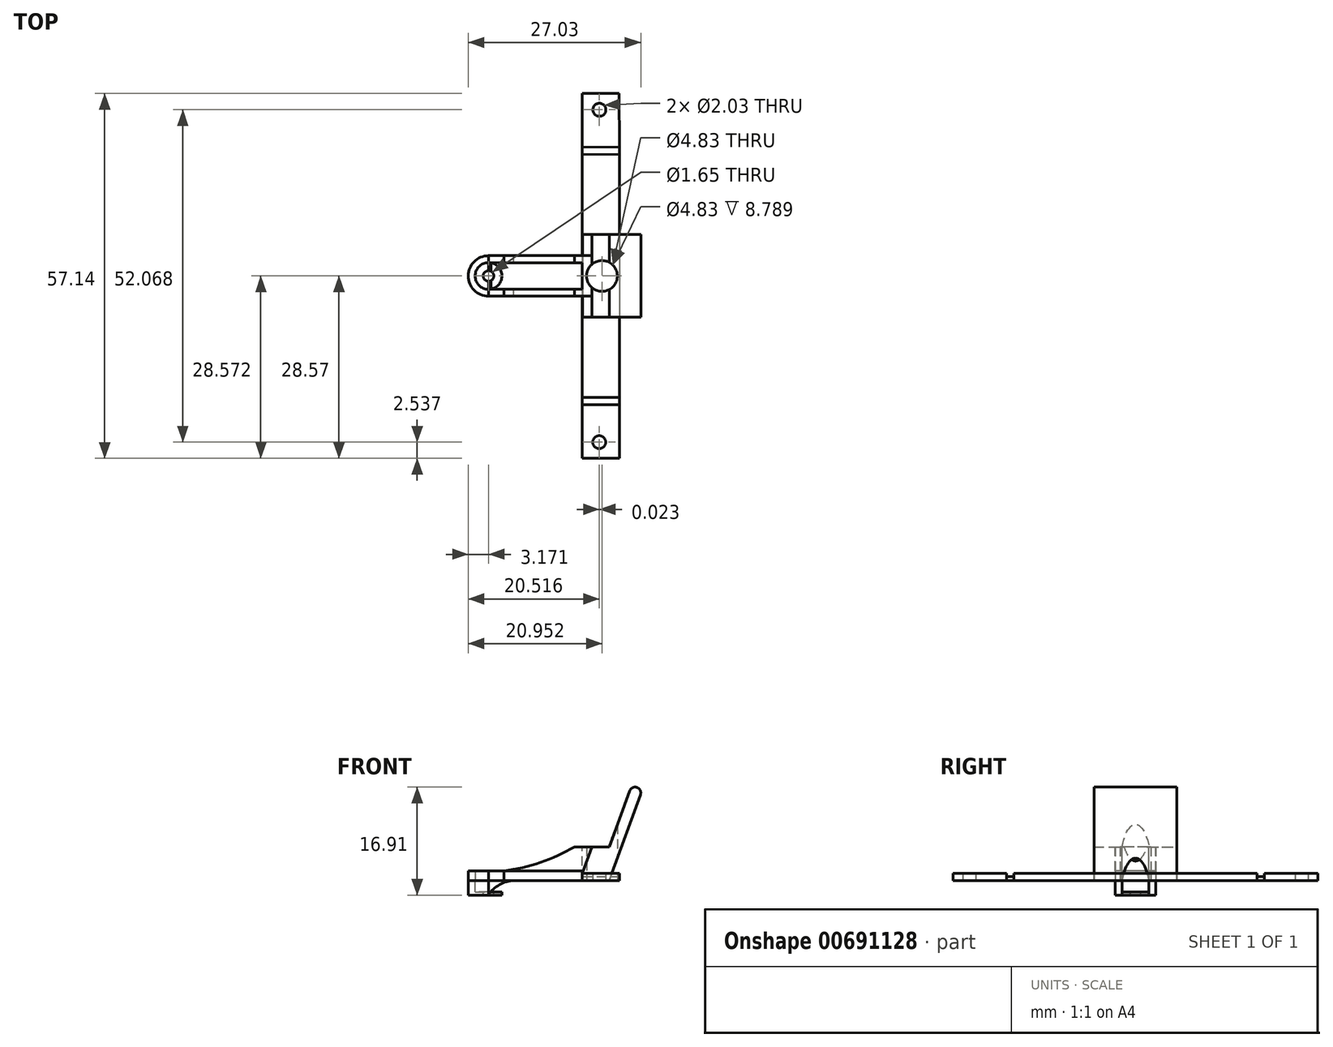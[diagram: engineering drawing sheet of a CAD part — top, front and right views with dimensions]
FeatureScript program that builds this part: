
annotation { "Feature Type Name" : "Feature", "Feature Type Description" : "" }
export const myFeature = defineFeature(function(context is Context, id is Id, definition is map)
    precondition{}
    {
        {
            var Q0;
            Q0=qCreatedBy(makeId("Top.planeOp"),FACE);
            var sketch = newSketch(context, id + "F0", { "sketchPlane" : qUnion([Q0])});
            skArc(sketch, "E0", {"start": v(-9.2, 3.18) * mm, "mid": v(-12.38, 0) * mm, "end": v(-9.2, -3.18) * mm});
            skCircle(sketch, "E1", {"center": v(-9.2, 0) * mm, "radius": 2.1 * mm});
            skLineSegment(sketch, "E2", {"start": v(11.34, 14.51) * mm, "end": v(11.34, -21.1) * mm});
            skLineSegment(sketch, "E3", {"start": v(5.47, 17.15) * mm, "end": v(5.47, -18.87) * mm});
            skCircle(sketch, "E4", {"center": v(-9.2, 0) * mm, "radius": 0.83 * mm});
            skLineSegment(sketch, "E5", {"start": v(-9.2, -3.17) * mm, "end": v(5.47, -3.17) * mm});
            skLineSegment(sketch, "E6", {"start": v(-9.2, 3.17) * mm, "end": v(5.47, 3.17) * mm});
            skLineSegment(sketch, "E7.trimOffspring", {"start": v(-6.81, -2.08) * mm, "end": v(5.47, -2.08) * mm});
            skLineSegment(sketch, "E8.trimOffspring", {"start": v(-6.81, 2.08) * mm, "end": v(5.47, 2.08) * mm});
            skPoint(sketch, "E9.start.orphan", {"position": v(-9.2, 2.1) * mm});
            skPoint(sketch, "E10.start.orphan", {"position": v(-9.2, -2.1) * mm});
            skCircle(sketch, "E11", {"center": v(8.57, 0) * mm, "radius": 2.41 * mm});
            skLineSegment(sketch, "E12", {"start": v(5.47, 17.15) * mm, "end": v(5.47, 28.57) * mm});
            skLineSegment(sketch, "E13", {"start": v(5.47, 28.57) * mm, "end": v(11.23, 28.57) * mm});
            skLineSegment(sketch, "E14", {"start": v(11.23, 28.57) * mm, "end": v(11.34, 14.51) * mm});
            skCircle(sketch, "E15", {"center": v(8.16, 26.03) * mm, "radius": 1.02 * mm});
            skLineSegment(sketch, "E16", {"start": v(5.47, -18.87) * mm, "end": v(5.47, -28.57) * mm});
            skLineSegment(sketch, "E17", {"start": v(5.47, -28.57) * mm, "end": v(11.34, -28.57) * mm});
            skLineSegment(sketch, "E18", {"start": v(11.34, -28.57) * mm, "end": v(11.34, -21.1) * mm});
            skCircle(sketch, "E19", {"center": v(8.14, -26.03) * mm, "radius": 1.02 * mm});
            skLineSegment(sketch, "E20", {"start": v(5.47, -19.05) * mm, "end": v(11.34, -19.05) * mm});
            skLineSegment(sketch, "E21", {"start": v(5.47, -20.2) * mm, "end": v(11.34, -20.2) * mm});
            skLineSegment(sketch, "E22", {"start": v(5.47, 19.03) * mm, "end": v(11.34, 19.07) * mm});
            skLineSegment(sketch, "E23", {"start": v(5.47, 20.17) * mm, "end": v(11.3, 20.22) * mm});
            skLineSegment(sketch, "E24", {"start": v(-6.81, -2.08) * mm, "end": v(-9.28, -2.1) * mm});
            skPoint(sketch, "E25.end.orphan", {"position": v(-9.7, 2.07) * mm});
            skPoint(sketch, "E26.orphan", {"position": v(-9.23, 3.17) * mm});
            skLineSegment(sketch, "E27", {"start": v(-6.81, 2.08) * mm, "end": v(-9.2, 2.1) * mm});
            skLineSegment(sketch, "E28", {"start": v(-9.2, -2.1) * mm, "end": v(-9.2, -3.18) * mm});
            skLineSegment(sketch, "E29", {"start": v(-9.2, 2.1) * mm, "end": v(-9.2, 3.18) * mm});
            skSolve(sketch);
        }
        {
            var Q0;
            Q0=qCreatedBy(makeId("Front.planeOp"),FACE);
            var sketch = newSketch(context, id + "F1", { "sketchPlane" : qUnion([Q0])});
            skLineSegment(sketch, "E30", {"start": v(4.23, 5.27) * mm, "end": v(9.7, 5.27) * mm});
            skLineSegment(sketch, "E31", {"start": v(9.7, 5.27) * mm, "end": v(13.44, 15.54) * mm});
            skLineSegment(sketch, "E32", {"start": v(14.6, 13.41) * mm, "end": v(9.7, 0) * mm});
            skLineSegment(sketch, "E33", {"start": v(5.52, 0) * mm, "end": v(9.7, 0) * mm});
            skLineSegment(sketch, "E34", {"start": v(5.52, 0) * mm, "end": v(-9.95, 0) * mm});
            skLineSegment(sketch, "E35", {"start": v(-6.76, 0) * mm, "end": v(-6.76, 1.52) * mm});
            skLineSegment(sketch, "E36", {"start": v(-6.76, 0) * mm, "end": v(9.7, 0) * mm});
            skLineSegment(sketch, "E37", {"start": v(6.97, 5.27) * mm, "end": v(5.51, 1.27) * mm});
            skArc(sketch, "E38", {"start": v(14.6, 13.41) * mm, "mid": v(14.05, 14.57) * mm, "end": v(12.9, 14.03) * mm});
            skPoint(sketch, "E39", {"position": v(13.44, 15.54) * mm});
            skArc(sketch, "E40", {"start": v(-6.76, 1.52) * mm, "mid": v(-1.06, 2.8) * mm, "end": v(4.23, 5.27) * mm});
            skLineSegment(sketch, "E41", {"start": v(-9.22, 0) * mm, "end": v(-9.22, -2.29) * mm});
            skLineSegment(sketch, "E42", {"start": v(-9.22, 0) * mm, "end": v(-6.76, 0) * mm});
            skArc(sketch, "E43", {"start": v(-5.25, 0) * mm, "mid": v(-7.5, -0.67) * mm, "end": v(-9.22, -2.29) * mm});
            skLineSegment(sketch, "E44", {"start": v(5.51, 0) * mm, "end": v(5.51, 1.27) * mm});
            skPoint(sketch, "E45.orphan", {"position": v(5.05, 0) * mm});
            skSolve(sketch);
        }
        {
            var Q0;
            {var subQ1=sQuery(id+"F0.wireOp",EDGE,"E13");Q0=makeQuery(id+"F0.imprint","IMPRINT",FACE,{"disambiguationData":[TD([[makeQuery(id+"F0.imprint","IMPRINT",EDGE,{"derivedFrom":subQ1}),-1.0]])]});}
            var Q1;
            {var subQ1=sQuery(id+"F0.wireOp",EDGE,"E17");Q1=makeQuery(id+"F0.imprint","IMPRINT",FACE,{"disambiguationData":[TD([[makeQuery(id+"F0.imprint","IMPRINT",EDGE,{"derivedFrom":subQ1}),1.0]])]});}
            var Q2;
            Q2=makeQuery(id+"F0.imprint","IMPRINT",FACE,{"disambiguationData":[TD([[makeQuery(id+"F0.imprint","IMPRINT",EDGE,{"derivedFrom":sQuery(id+"F0.wireOp",EDGE,"E11")}),-1.0]])]});
            extrude(context, id + "F2", {"entities" : qUnion([Q0, Q1, Q2]), "depth" : 1.14 * mm, "offsetDistance" : 25.4 * mm});
        }
        {
            var Q0;
            {var subQ1=sQuery(id+"F1.wireOp",EDGE,"E35");Q0=makeQuery(id+"F1.imprint","IMPRINT",FACE,{"disambiguationData":[TD([[makeQuery(id+"F1.imprint","IMPRINT",EDGE,{"derivedFrom":subQ1}),-1.0]])]});}
            extrude(context, id + "F3", {"entities" : qUnion([Q0]), "operationType" : NewBodyOperationType.ADD, "endBound" : BoundingType.SYMMETRIC, "depth" : 6.35 * mm, "offsetDistance" : 25.4 * mm});
        }
        {
            var Q0;
            {var subQ0=sQuery(id+"F0.wireOp",EDGE,"E8.trimOffspring");Q0=makeQuery(id+"F0.imprint","IMPRINT",FACE,{"disambiguationData":[TD([[makeQuery(id+"F0.imprint","IMPRINT",EDGE,{"derivedFrom":subQ0}),1.0]])]});}
            var Q1;
            {var subQ0=sQuery(id+"F0.wireOp",EDGE,"E7.trimOffspring");Q1=makeQuery(id+"F0.imprint","IMPRINT",FACE,{"disambiguationData":[TD([[makeQuery(id+"F0.imprint","IMPRINT",EDGE,{"derivedFrom":subQ0}),-1.0]])]});}
            extrude(context, id + "F4", {"entities" : qUnion([Q0, Q1]), "depth" : 1.52 * mm, "offsetDistance" : 25.4 * mm});
        }
        {
            var Q0;
            {var subQ0=sQuery(id+"F0.wireOp",EDGE,"E7.trimOffspring");Q0=makeQuery(id+"F0.imprint","IMPRINT",FACE,{"disambiguationData":[TD([[makeQuery(id+"F0.imprint","IMPRINT",EDGE,{"derivedFrom":subQ0}),1.0]])]});}
            extrude(context, id + "F5", {"entities" : qUnion([Q0]), "operationType" : NewBodyOperationType.REMOVE, "endBound" : BoundingType.SYMMETRIC, "oppositeDirection" : true, "depth" : 25.4 * mm, "offsetDistance" : 25.4 * mm});
        }
        {
            var Q0;
            {var subQ0=sQuery(id+"F1.wireOp",EDGE,"E32");Q0=makeQuery(id+"F1.imprint","IMPRINT",FACE,{"disambiguationData":[TD([[makeQuery(id+"F1.imprint","IMPRINT",EDGE,{"derivedFrom":subQ0}),-1.0]])]});}
            extrude(context, id + "F6", {"entities" : qUnion([Q0]), "endBound" : BoundingType.SYMMETRIC, "depth" : 12.95 * mm, "offsetDistance" : 25.4 * mm});
        }
        {
            var Q0;
            Q0=makeQuery(id+"F0.imprint","IMPRINT",FACE,{"disambiguationData":[TD([[makeQuery(id+"F0.imprint","IMPRINT",EDGE,{"derivedFrom":sQuery(id+"F0.wireOp",EDGE,"E11")}),1.0]])]});
            extrude(context, id + "F7", {"entities" : qUnion([Q0]), "operationType" : NewBodyOperationType.REMOVE, "oppositeDirection" : true, "depth" : -25.4 * mm, "offsetDistance" : 25.4 * mm});
        }
        {
            var Q0;
            {var subQ3=sQuery(id+"F0.wireOp",EDGE,"E23");Q0=makeQuery(id+"F0.imprint","IMPRINT",FACE,{"disambiguationData":[TD([[makeQuery(id+"F0.imprint","IMPRINT",EDGE,{"derivedFrom":subQ3}),-1.0]])]});}
            var Q1;
            {var subQ0=sQuery(id+"F0.wireOp",EDGE,"E20");Q1=makeQuery(id+"F0.imprint","IMPRINT",FACE,{"disambiguationData":[TD([[makeQuery(id+"F0.imprint","IMPRINT",EDGE,{"derivedFrom":subQ0}),-1.0]])]});}
            extrude(context, id + "F8", {"entities" : qUnion([Q0, Q1]), "depth" : 0.64 * mm, "offsetDistance" : 25.4 * mm});
        }
        {
            var Q0;
            Q0=makeQuery(id+"F0.imprint","IMPRINT",FACE,{"disambiguationData":[TD([[makeQuery(id+"F0.imprint","IMPRINT",EDGE,{"derivedFrom":sQuery(id+"F0.wireOp",EDGE,"E1")}),-1.0]])]});
            extrude(context, id + "F9", {"entities" : qUnion([Q0]), "depth" : 1.52 * mm, "offsetDistance" : 25.4 * mm});
        }
        {
            var Q0;
            Q0=makeQuery(id+"F0.imprint","IMPRINT",FACE,{"disambiguationData":[TD([[makeQuery(id+"F0.imprint","IMPRINT",EDGE,{"derivedFrom":sQuery(id+"F0.wireOp",EDGE,"E4")}),-1.0]])]});
            var Q1;
            {var subQ1=sQuery(id+"F0.wireOp",EDGE,"E0");var subQ3=sQuery(id+"F0.wireOp",EDGE,"E5");var subQ5=makeQuery(id+"F0.imprint","INTERSECT",VERTEX,{"disambiguationData":[OD(0.0)],"derivedFrom":[subQ1,subQ3]});Q1=makeQuery(id+"F0.imprint","IMPRINT",FACE,{"disambiguationData":[TD([[makeQuery(id+"F0.imprint","IMPRINT",EDGE,{"disambiguationData":[TD([[subQ5,1.0]])],"derivedFrom":subQ1}),1.0]])]});}
            var Q2;
            {var subQ8=sQuery(id+"F0.wireOp",EDGE,"vhmCoDp7-a18j-IEBU-yVJi-eEU0BIF8JmBv");Q2=makeQuery(id+"F0.imprint","IMPRINT",FACE,{"disambiguationData":[TD([[makeQuery(id+"F0.imprint","IMPRINT",EDGE,{"derivedFrom":subQ8}),-1.0]])]});}
            extrude(context, id + "F10", {"entities" : qUnion([Q0, Q1, Q2]), "oppositeDirection" : true, "depth" : 2.3 * mm, "offsetDistance" : 25.4 * mm});
        }
        {
            var Q0;
            Q0=makeQuery(id+"F1.imprint","IMPRINT",FACE,{"disambiguationData":[TD([[makeQuery(id+"F1.imprint","IMPRINT",EDGE,{"derivedFrom":sQuery(id+"F1.wireOp",EDGE,"E41")}),1.0]])]});
            extrude(context, id + "F11", {"entities" : qUnion([Q0]), "endBound" : BoundingType.SYMMETRIC, "depth" : 6.35 * mm, "offsetDistance" : 25.4 * mm});
        }
        {
            var Q0;
            Q0=makeQuery(id+"F0.imprint","IMPRINT",FACE,{"disambiguationData":[TD([[makeQuery(id+"F0.imprint","IMPRINT",EDGE,{"derivedFrom":sQuery(id+"F0.wireOp",EDGE,"E4")}),-1.0]])]});
            extrude(context, id + "F12", {"entities" : qUnion([Q0]), "operationType" : NewBodyOperationType.REMOVE, "flatOperationType" : FlatOperationType.REMOVE, "oppositeDirection" : true, "depth" : 1.78 * mm, "offsetDistance" : 25.4 * mm, "domain" : OperationDomain.MODEL});
        }
        {
            var Q0;
            {var subQ2=sQuery(id+"F0.wireOp",EDGE,"E7.trimOffspring");Q0=makeQuery(id+"F0.imprint","IMPRINT",FACE,{"disambiguationData":[TD([[makeQuery(id+"F0.imprint","IMPRINT",EDGE,{"derivedFrom":subQ2}),1.0]])]});}
            var Q1;
            Q1=makeQuery(id+"F0.imprint","IMPRINT",FACE,{"disambiguationData":[TD([[makeQuery(id+"F0.imprint","IMPRINT",EDGE,{"derivedFrom":sQuery(id+"F0.wireOp",EDGE,"E4")}),1.0]])]});
            extrude(context, id + "F13", {"entities" : qUnion([Q0, Q1]), "operationType" : NewBodyOperationType.REMOVE, "oppositeDirection" : true, "depth" : 25.4 * mm, "offsetDistance" : 25.4 * mm});
        }
    });
